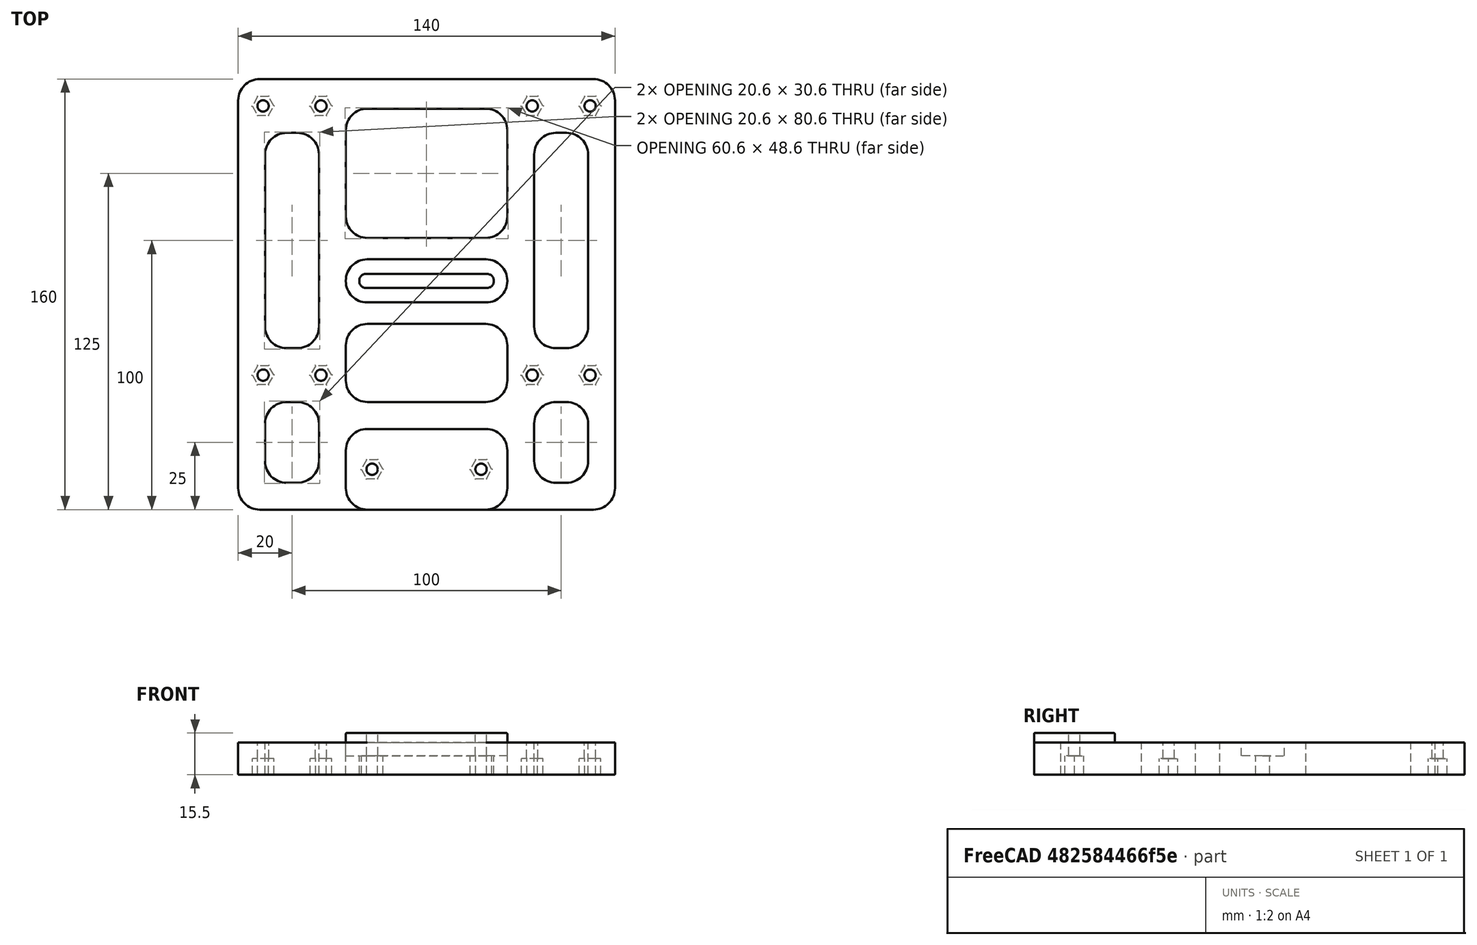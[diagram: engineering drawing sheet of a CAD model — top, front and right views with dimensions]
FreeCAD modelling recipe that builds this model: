
FCSTD DOCUMENT  (FreeCAD 0.18R16131 (Git))
Label: X_Grundplatte_Ende_Ver2
License: All rights reserved
LicenseURL: http://en.wikipedia.org/wiki/All_rights_reserved
objects: Part::Cut×28, Part::Fillet×13, Part::Box×10, Part::Cylinder×10, Part::Part2DObjectPython×10, Part::Extrusion×10, Part::MultiFuse×1
note: 82 computed .brp shape members not serialized (recipe doc carries the construction recipe); baked Part::Feature solids carry a one-line shape summary decoded from their .brp

FEATURE [Part::Box] Box  label="Würfel"
  AttacherType = Attacher::AttachEngine3D
  Height = 12
  Length = 140
  Width = 160
FEATURE [Part::Box] Box007  label="Würfel007"
  AttacherType = Attacher::AttachEngine3D
  Height = 20
  Length = 60
  Placement = pos=(40,101,0) rot=(0,0,1;0rad)
  Width = 48
FEATURE [Part::Box] Box008  label="Würfel008"
  AttacherType = Attacher::AttachEngine3D
  Height = 20
  Length = 20
  Placement = pos=(10,60,0) rot=(0,0,1;0rad)
  Width = 80
FEATURE [Part::Box] Box009  label="Würfel009"
  AttacherType = Attacher::AttachEngine3D
  Height = 20
  Length = 20
  Placement = pos=(110,60,0) rot=(0,0,1;0rad)
  Width = 80
FEATURE [Part::Box] Box010  label="Würfel010"
  AttacherType = Attacher::AttachEngine3D
  Height = 20
  Length = 20
  Placement = pos=(10,10,0) rot=(0,0,1;0rad)
  Width = 30
FEATURE [Part::Box] Box011  label="Würfel011"
  AttacherType = Attacher::AttachEngine3D
  Height = 20
  Length = 20
  Placement = pos=(110,10,0) rot=(0,0,1;0rad)
  Width = 30
FEATURE [Part::Cylinder] Cylinder006  label="Bohrung001"
  Angle = 360
  AttacherType = Attacher::AttachEngine3D
  Height = 20
  Placement = pos=(9.25,50,0) rot=(0,0,1;0rad)
  Radius = 2.1
FEATURE [Part::Cylinder] Cylinder007  label="Bohrung002"
  Angle = 360
  AttacherType = Attacher::AttachEngine3D
  Height = 20
  Placement = pos=(9.25,150,0) rot=(0,0,1;0rad)
  Radius = 2.1
FEATURE [Part::Cylinder] Cylinder008  label="Bohrung003"
  Angle = 360
  AttacherType = Attacher::AttachEngine3D
  Height = 20
  Placement = pos=(30.75,50,0) rot=(0,0,1;0rad)
  Radius = 2.1
FEATURE [Part::Cylinder] Cylinder009  label="Bohrung004"
  Angle = 360
  AttacherType = Attacher::AttachEngine3D
  Height = 20
  Placement = pos=(30.75,150,0) rot=(0,0,1;0rad)
  Radius = 2.1
FEATURE [Part::Cylinder] Cylinder010  label="Bohrung005"
  Angle = 360
  AttacherType = Attacher::AttachEngine3D
  Height = 20
  Placement = pos=(130.75,150,0) rot=(0,0,1;0rad)
  Radius = 2.1
FEATURE [Part::Cylinder] Cylinder011  label="Bohrung006"
  Angle = 360
  AttacherType = Attacher::AttachEngine3D
  Height = 20
  Placement = pos=(109.25,150,0) rot=(0,0,1;0rad)
  Radius = 2.1
FEATURE [Part::Cylinder] Cylinder012  label="Bohrung007"
  Angle = 360
  AttacherType = Attacher::AttachEngine3D
  Height = 20
  Placement = pos=(109.25,50,0) rot=(0,0,1;0rad)
  Radius = 2.1
FEATURE [Part::Cylinder] Cylinder013  label="Bohrung008"
  Angle = 360
  AttacherType = Attacher::AttachEngine3D
  Height = 20
  Placement = pos=(130.75,50,0) rot=(0,0,1;0rad)
  Radius = 2.1
FEATURE [Part::Part2DObjectPython] Polygon  # Draft 2D object (typed FeaturePython)
  ChamferSize = 0
  DrawMode = 0
  FacesNumber = 6
  FilletRadius = 0
  MakeFace = true
  Radius = 4
FEATURE [Part::Extrusion] Extrude  label="Mutter001"
  Base = -> Polygon
  Dir = (0,0,1)
  DirMode = 2
  FaceMakerClass = Part::FaceMakerBullseye
  LengthFwd = 6
  LengthRev = 0
  Placement = pos=(9.25,50,0) rot=(0,0,1;0rad)
  Solid = false
  Symmetric = false
FEATURE [Part::Part2DObjectPython] Polygon001  # Draft 2D object (typed FeaturePython)
  ChamferSize = 0
  DrawMode = 0
  FacesNumber = 6
  FilletRadius = 0
  MakeFace = true
  Radius = 4
FEATURE [Part::Extrusion] Extrude001  label="Mutter002"
  Base = -> Polygon001
  Dir = (0,0,1)
  DirMode = 2
  FaceMakerClass = Part::FaceMakerBullseye
  LengthFwd = 6
  LengthRev = 0
  Placement = pos=(9.25,150,0) rot=(0,0,1;0rad)
  Solid = false
  Symmetric = false
FEATURE [Part::Part2DObjectPython] Polygon002  # Draft 2D object (typed FeaturePython)
  ChamferSize = 0
  DrawMode = 0
  FacesNumber = 6
  FilletRadius = 0
  MakeFace = true
  Radius = 4
FEATURE [Part::Extrusion] Extrude002  label="Mutter003"
  Base = -> Polygon002
  Dir = (0,0,1)
  DirMode = 2
  FaceMakerClass = Part::FaceMakerBullseye
  LengthFwd = 6
  LengthRev = 0
  Placement = pos=(30.75,50,0) rot=(0,0,1;0rad)
  Solid = false
  Symmetric = false
FEATURE [Part::Part2DObjectPython] Polygon003  # Draft 2D object (typed FeaturePython)
  ChamferSize = 0
  DrawMode = 0
  FacesNumber = 6
  FilletRadius = 0
  MakeFace = true
  Radius = 4
FEATURE [Part::Extrusion] Extrude003  label="Mutter004"
  Base = -> Polygon003
  Dir = (0,0,1)
  DirMode = 2
  FaceMakerClass = Part::FaceMakerBullseye
  LengthFwd = 6
  LengthRev = 0
  Placement = pos=(30.75,150,0) rot=(0,0,1;0rad)
  Solid = false
  Symmetric = false
FEATURE [Part::Part2DObjectPython] Polygon004  # Draft 2D object (typed FeaturePython)
  ChamferSize = 0
  DrawMode = 0
  FacesNumber = 6
  FilletRadius = 0
  MakeFace = true
  Radius = 4
FEATURE [Part::Extrusion] Extrude004  label="Mutter005"
  Base = -> Polygon004
  Dir = (0,0,1)
  DirMode = 2
  FaceMakerClass = Part::FaceMakerBullseye
  LengthFwd = 6
  LengthRev = 0
  Placement = pos=(130.75,50,0) rot=(0,0,1;0rad)
  Solid = false
  Symmetric = false
FEATURE [Part::Part2DObjectPython] Polygon005  # Draft 2D object (typed FeaturePython)
  ChamferSize = 0
  DrawMode = 0
  FacesNumber = 6
  FilletRadius = 0
  MakeFace = true
  Radius = 4
FEATURE [Part::Extrusion] Extrude005  label="Mutter006"
  Base = -> Polygon005
  Dir = (0,0,1)
  DirMode = 2
  FaceMakerClass = Part::FaceMakerBullseye
  LengthFwd = 6
  LengthRev = 0
  Placement = pos=(130.75,150,0) rot=(0,0,1;0rad)
  Solid = false
  Symmetric = false
FEATURE [Part::Part2DObjectPython] Polygon006  # Draft 2D object (typed FeaturePython)
  ChamferSize = 0
  DrawMode = 0
  FacesNumber = 6
  FilletRadius = 0
  MakeFace = true
  Radius = 4
FEATURE [Part::Extrusion] Extrude006  label="Mutter007"
  Base = -> Polygon006
  Dir = (0,0,1)
  DirMode = 2
  FaceMakerClass = Part::FaceMakerBullseye
  LengthFwd = 6
  LengthRev = 0
  Placement = pos=(109.25,150,0) rot=(0,0,1;0rad)
  Solid = false
  Symmetric = false
FEATURE [Part::Part2DObjectPython] Polygon007  # Draft 2D object (typed FeaturePython)
  ChamferSize = 0
  DrawMode = 0
  FacesNumber = 6
  FilletRadius = 0
  MakeFace = true
  Radius = 4
FEATURE [Part::Extrusion] Extrude007  label="Mutter008"
  Base = -> Polygon007
  Dir = (0,0,1)
  DirMode = 2
  FaceMakerClass = Part::FaceMakerBullseye
  LengthFwd = 6
  LengthRev = 0
  Placement = pos=(109.25,50,0) rot=(0,0,1;0rad)
  Solid = false
  Symmetric = false
FEATURE [Part::Cut] Cut
  Base = -> Box
  Tool = -> Cylinder006
FEATURE [Part::Cut] Cut001
  Base = -> Cut
  Tool = -> Extrude007
FEATURE [Part::Cut] Cut002
  Base = -> Cut001
  Tool = -> Extrude006
FEATURE [Part::Cut] Cut003
  Base = -> Cut002
  Tool = -> Extrude005
FEATURE [Part::Cut] Cut004
  Base = -> Cut003
  Tool = -> Extrude004
FEATURE [Part::Cut] Cut005
  Base = -> Cut004
  Tool = -> Extrude003
FEATURE [Part::Cut] Cut006
  Base = -> Cut005
  Tool = -> Extrude002
FEATURE [Part::Cut] Cut007
  Base = -> Cut006
  Tool = -> Extrude001
FEATURE [Part::Cut] Cut008
  Base = -> Cut007
  Tool = -> Extrude
FEATURE [Part::Cut] Cut009
  Base = -> Cut008
  Tool = -> Cylinder013
FEATURE [Part::Cut] Cut010
  Base = -> Cut009
  Tool = -> Cylinder012
FEATURE [Part::Cut] Cut011
  Base = -> Cut010
  Tool = -> Cylinder011
FEATURE [Part::Cut] Cut012
  Base = -> Cut011
  Tool = -> Cylinder010
FEATURE [Part::Fillet] Fillet
  Base = -> Box008
  Edges = 4 edges r=8: [Edge1,Edge3,Edge5,Edge7]
FEATURE [Part::Fillet] Fillet001
  Base = -> Box010
  Edges = 4 edges r=8: [Edge1,Edge3,Edge5,Edge7]
FEATURE [Part::Fillet] Fillet002
  Base = -> Box009
  Edges = 4 edges r=8: [Edge1,Edge3,Edge5,Edge7]
FEATURE [Part::Fillet] Fillet003
  Base = -> Box011
  Edges = 4 edges r=8: [Edge1,Edge3,Edge5,Edge7]
FEATURE [Part::Box] Box013  label="Würfel013"
  AttacherType = Attacher::AttachEngine3D
  Height = 20
  Length = 60
  Placement = pos=(40,77,7) rot=(0,0,1;0rad)
  Width = 16
FEATURE [Part::Fillet] Fillet004
  Base = -> Box013
  Edges = 4 edges r=7.9: [Edge1,Edge3,Edge5,Edge7]
FEATURE [Part::Box] Box014  label="Würfel014"
  AttacherType = Attacher::AttachEngine3D
  Height = 20
  Length = 50
  Placement = pos=(45,82.4,0) rot=(0,0,1;0rad)
  Width = 5.2
FEATURE [Part::Fillet] Fillet005
  Base = -> Box014
  Edges = 4 edges r=2.5: [Edge1,Edge3,Edge5,Edge7]
FEATURE [Part::Fillet] Fillet006
  Base = -> Box007
  Edges = 4 edges r=8: [Edge1,Edge3,Edge5,Edge7]
FEATURE [Part::Cut] Cut013
  Base = -> Cut012
  Tool = -> Cylinder009
FEATURE [Part::Cut] Cut014
  Base = -> Cut013
  Tool = -> Cylinder008
FEATURE [Part::Cut] Cut015
  Base = -> Cut014
  Tool = -> Cylinder007
FEATURE [Part::Cut] Cut016
  Base = -> Cut015
  Tool = -> Fillet003
FEATURE [Part::Cut] Cut017
  Base = -> Cut016
  Tool = -> Fillet002
FEATURE [Part::Cut] Cut018
  Base = -> Cut017
  Tool = -> Fillet001
FEATURE [Part::Cut] Cut019
  Base = -> Cut018
  Tool = -> Fillet
FEATURE [Part::Cut] Cut020
  Base = -> Cut019
  Tool = -> Fillet004
FEATURE [Part::Cut] Cut021
  Base = -> Cut020
  Tool = -> Fillet005
FEATURE [Part::Cut] Cut022
  Base = -> Cut021
  Tool = -> Fillet006
FEATURE [Part::Box] Box001  label="Würfel001"
  AttacherType = Attacher::AttachEngine3D
  Height = 15.5
  Length = 60
  Placement = pos=(40,0,0) rot=(0,0,1;0rad)
  Width = 30
FEATURE [Part::Box] Box015  label="Würfel015"
  AttacherType = Attacher::AttachEngine3D
  Height = 30
  Length = 60
  Placement = pos=(40,40,0) rot=(0,0,1;0rad)
  Width = 29
FEATURE [Part::Fillet] Fillet007
  Base = -> Box015
  Edges = 4 edges r=8: [Edge1,Edge3,Edge5,Edge7]
FEATURE [Part::Cut] Cut023
  Base = -> Cut022
  Tool = -> Fillet007
FEATURE [Part::Fillet] Fillet008
  Base = -> Box001
  Edges = 4 edges r=8: [Edge1,Edge3,Edge5,Edge7]
FEATURE [Part::MultiFuse] Fusion
  Shapes = -> [Fillet008,Cut023]
FEATURE [Part::Cylinder] Cylinder  label="Zylinder"
  Angle = 360
  AttacherType = Attacher::AttachEngine3D
  Height = 30
  Placement = pos=(49.75,15,0) rot=(0,0,1;0rad)
  Radius = 2.1
FEATURE [Part::Cylinder] Cylinder014  label="Zylinder001"
  Angle = 360
  AttacherType = Attacher::AttachEngine3D
  Height = 30
  Placement = pos=(90.25,15,0) rot=(0,0,1;0rad)
  Radius = 2.1
FEATURE [Part::Part2DObjectPython] Polygon008  # Draft 2D object (typed FeaturePython)
  ChamferSize = 0
  DrawMode = 0
  FacesNumber = 6
  FilletRadius = 0
  MakeFace = true
  Radius = 4
FEATURE [Part::Extrusion] Extrude008
  Base = -> Polygon008
  Dir = (0,0,1)
  DirMode = 2
  FaceMakerClass = Part::FaceMakerBullseye
  LengthFwd = 7
  LengthRev = 0
  Placement = pos=(49.75,15,0) rot=(0,0,1;0rad)
  Solid = false
  Symmetric = false
FEATURE [Part::Part2DObjectPython] Polygon009  # Draft 2D object (typed FeaturePython)
  ChamferSize = 0
  DrawMode = 0
  FacesNumber = 6
  FilletRadius = 0
  MakeFace = true
  Radius = 4
FEATURE [Part::Extrusion] Extrude009
  Base = -> Polygon009
  Dir = (0,0,1)
  DirMode = 2
  FaceMakerClass = Part::FaceMakerBullseye
  LengthFwd = 7
  LengthRev = 0
  Placement = pos=(90.25,15,0) rot=(0,0,1;0rad)
  Solid = false
  Symmetric = false
FEATURE [Part::Cut] Cut024
  Base = -> Fusion
  Tool = -> Cylinder
FEATURE [Part::Cut] Cut025
  Base = -> Cut024
  Tool = -> Cylinder014
FEATURE [Part::Cut] Cut026
  Base = -> Cut025
  Tool = -> Extrude009
FEATURE [Part::Cut] Cut027
  Base = -> Cut026
  Tool = -> Extrude008
FEATURE [Part::Fillet] Fillet009
  Base = -> Cut027
  Edges = 4 edges r=8: [Edge101,Edge102,Edge103,Edge109]
FEATURE [Part::Fillet] Fillet010
  Base = -> Fillet009
  Edges = 136 edges r=0.3: [Edge81,Edge84,Edge86,Edge89,Edge91,Edge92,Edge94,Edge96,Edge98,Edge116,Edge119,Edge121,Edge122,Edge125,Edge127,Edge128,Edge131,Edge132,Edge135,Edge137,Edge138,Edge141,Edge143,Edge144,Edge147,Edge148,Edge150,Edge153,Edge155,Edge156,Edge159,Edge161,Edge162,Edge165,Edge166,Edge168,Edge170,Edge173,+98 more]
FEATURE [Part::Fillet] Fillet011
  Base = -> Fillet010
  Edges = 72 edges r=0.3: [Edge25,Edge26,Edge27,Edge28,Edge29,Edge30,Edge31,Edge32,Edge33,Edge34,Edge35,Edge36,Edge37,Edge38,Edge39,Edge40,Edge41,Edge42,Edge43,Edge44,Edge45,Edge46,Edge47,Edge48,Edge49,Edge50,Edge51,Edge52,Edge53,Edge54,Edge55,Edge56,Edge57,Edge58,Edge59,Edge60,Edge61,Edge62,Edge63,Edge64,Edge65,Edge66,+30 more]
FEATURE [Part::Fillet] Fillet012
  Base = -> Fillet011
  Edges = 10 edges r=0.3: [Edge105,Edge108,Edge110,Edge112,Edge114,Edge116,Edge118,Edge272,Edge273,Edge274]
